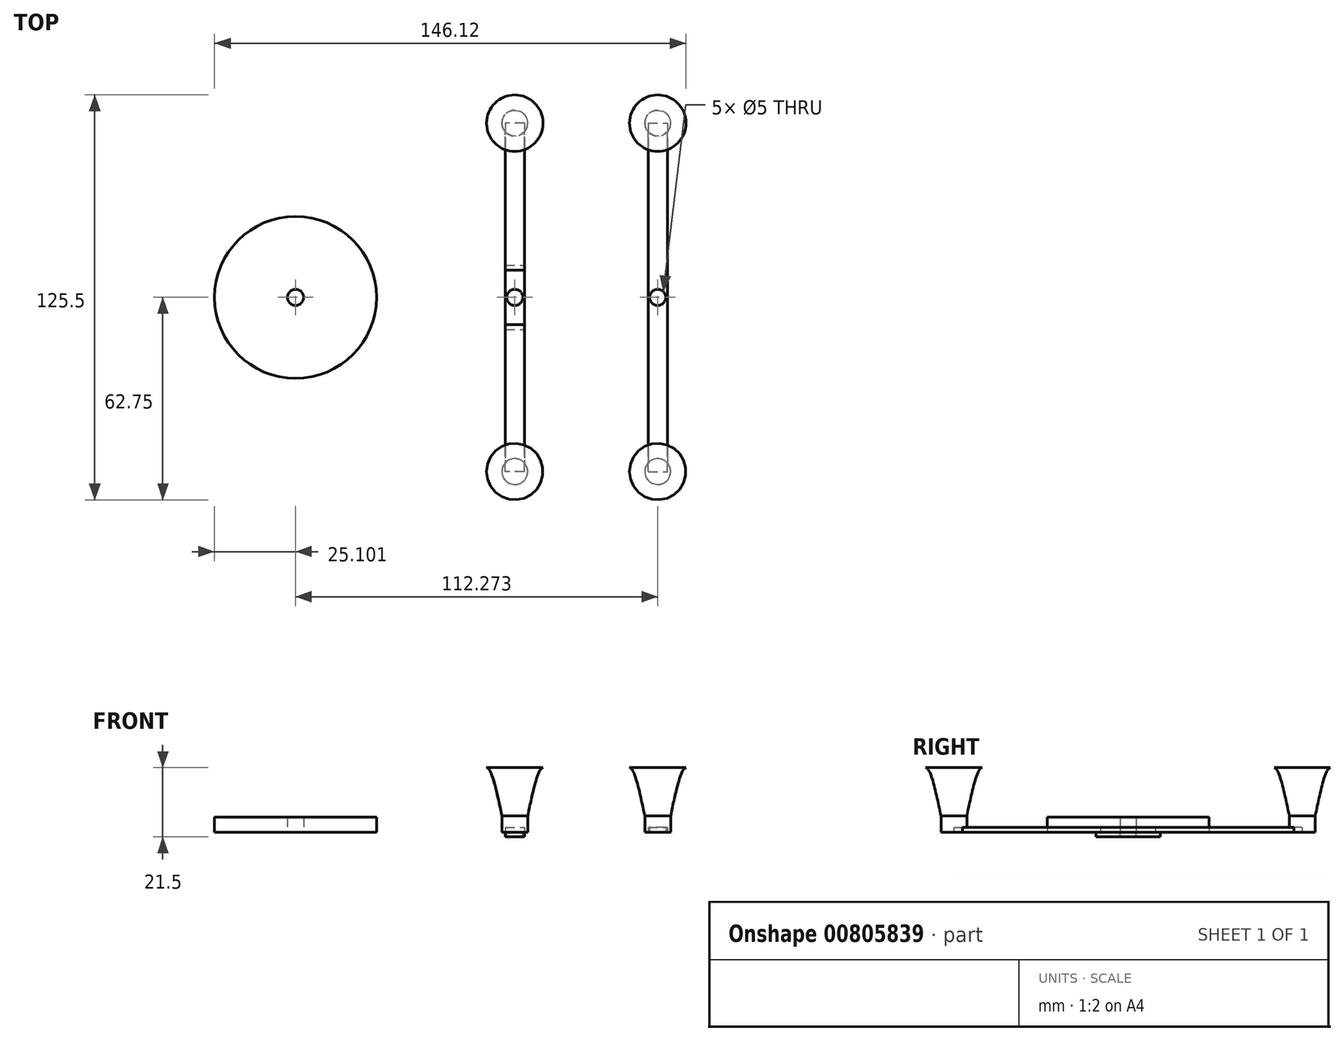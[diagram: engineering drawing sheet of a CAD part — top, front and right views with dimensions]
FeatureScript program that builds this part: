
annotation { "Feature Type Name" : "Feature", "Feature Type Description" : "" }
export const myFeature = defineFeature(function(context is Context, id is Id, definition is map)
    precondition{}
    {
        {
            var Q0;
            Q0=qCreatedBy(makeId("Top.planeOp"),FACE);
            var sketch = newSketch(context, id + "F0", { "sketchPlane" : qUnion([Q0])});
            skLineSegment(sketch, "E0.bottom", {"start": v(3, -54) * mm, "end": v(-3, -54) * mm});
            skLineSegment(sketch, "E0.top", {"start": v(3, 54) * mm, "end": v(-3, 54) * mm});
            skLineSegment(sketch, "E0.left", {"start": v(3, -54) * mm, "end": v(3, 54) * mm});
            skLineSegment(sketch, "E0.right", {"start": v(-3, -54) * mm, "end": v(-3, 54) * mm});
            skPoint(sketch, "E0.middle", {"position": v(0, 0) * mm});
            skCircle(sketch, "E1", {"center": v(0, 0) * mm, "radius": 2.5 * mm});
            skLineSegment(sketch, "E2", {"start": v(-3, 10) * mm, "end": v(3, 10) * mm});
            skLineSegment(sketch, "E3.MirrorCS", {"start": v(-3, -10) * mm, "end": v(3, -10) * mm});
            skLineSegment(sketch, "E4", {"start": v(-3, 8.5) * mm, "end": v(3, 8.5) * mm});
            skLineSegment(sketch, "E5.MirrorCS", {"start": v(-3, -8.5) * mm, "end": v(3, -8.5) * mm});
            skLineSegment(sketch, "E6.bottom", {"start": v(41.3, -54) * mm, "end": v(47.3, -54) * mm});
            skLineSegment(sketch, "E6.top", {"start": v(41.3, 54) * mm, "end": v(47.3, 54) * mm});
            skLineSegment(sketch, "E6.left", {"start": v(41.3, -54) * mm, "end": v(41.3, 54) * mm});
            skLineSegment(sketch, "E6.right", {"start": v(47.3, -54) * mm, "end": v(47.3, 54) * mm});
            skPoint(sketch, "E6.middle", {"position": v(44.3, 0) * mm});
            skCircle(sketch, "E7", {"center": v(44.3, 0) * mm, "radius": 2.5 * mm});
            skCircle(sketch, "E8", {"center": v(-67.97, 0) * mm, "radius": 25.1 * mm});
            skCircle(sketch, "E9", {"center": v(-67.97, 0) * mm, "radius": 2.5 * mm});
            skCircle(sketch, "E10", {"center": v(44.3, 54) * mm, "radius": 4 * mm});
            skCircle(sketch, "E11", {"center": v(0, 54) * mm, "radius": 4 * mm});
            skSolve(sketch);
        }
        {
            var Q0;
            {var subQ0=sQuery(id+"F0.wireOp",EDGE,"E0.top");Q0=makeQuery(id+"F0.imprint","IMPRINT",FACE,{"disambiguationData":[TD([[makeQuery(id+"F0.imprint","IMPRINT",EDGE,{"derivedFrom":subQ0}),1.0]])]});}
            var Q1;
            {var subQ0=sQuery(id+"F0.wireOp",EDGE,"E0.bottom");Q1=makeQuery(id+"F0.imprint","IMPRINT",FACE,{"disambiguationData":[TD([[makeQuery(id+"F0.imprint","IMPRINT",EDGE,{"derivedFrom":subQ0}),-1.0]])]});}
            var Q2;
            {var subQ0=sQuery(id+"F0.wireOp",EDGE,"E2");Q2=makeQuery(id+"F0.imprint","IMPRINT",FACE,{"disambiguationData":[TD([[makeQuery(id+"F0.imprint","IMPRINT",EDGE,{"derivedFrom":subQ0}),-1.0]])]});}
            var Q3;
            {var subQ0=sQuery(id+"F0.wireOp",EDGE,"E3.MirrorCS");Q3=makeQuery(id+"F0.imprint","IMPRINT",FACE,{"disambiguationData":[TD([[makeQuery(id+"F0.imprint","IMPRINT",EDGE,{"derivedFrom":subQ0}),1.0]])]});}
            var Q4;
            Q4=makeQuery(id+"F0.imprint","IMPRINT",FACE,{"disambiguationData":[TD([[makeQuery(id+"F0.imprint","IMPRINT",EDGE,{"derivedFrom":sQuery(id+"F0.wireOp",EDGE,"E6.bottom")}),1.0]])]});
            var Q5;
            {var subQ0=sQuery(id+"F0.wireOp",EDGE,"E6.top");Q5=makeQuery(id+"F0.imprint","IMPRINT",FACE,{"disambiguationData":[TD([[makeQuery(id+"F0.imprint","IMPRINT",EDGE,{"derivedFrom":subQ0}),1.0]])]});}
            var Q6;
            {var subQ0=sQuery(id+"F0.wireOp",EDGE,"E6.top");Q6=makeQuery(id+"F0.imprint","IMPRINT",FACE,{"disambiguationData":[TD([[makeQuery(id+"F0.imprint","IMPRINT",EDGE,{"derivedFrom":subQ0}),-1.0]])]});}
            var Q7;
            {var subQ0=sQuery(id+"F0.wireOp",EDGE,"E2");Q7=makeQuery(id+"F0.imprint","IMPRINT",FACE,{"disambiguationData":[TD([[makeQuery(id+"F0.imprint","IMPRINT",EDGE,{"derivedFrom":subQ0}),1.0]])]});}
            var Q8;
            {var subQ0=sQuery(id+"F0.wireOp",EDGE,"E0.top");Q8=makeQuery(id+"F0.imprint","IMPRINT",FACE,{"disambiguationData":[TD([[makeQuery(id+"F0.imprint","IMPRINT",EDGE,{"derivedFrom":subQ0}),-1.0]])]});}
            extrude(context, id + "F1", {"entities" : qUnion([Q0, Q1, Q2, Q3, Q4, Q5, Q6, Q7, Q8]), "depth" : 1.5 * mm, "offsetDistance" : 25 * mm});
        }
        {
            var Q0;
            {var subQ0=sQuery(id+"F0.wireOp",EDGE,"E2");Q0=makeQuery(id+"F0.imprint","IMPRINT",FACE,{"disambiguationData":[TD([[makeQuery(id+"F0.imprint","IMPRINT",EDGE,{"derivedFrom":subQ0}),-1.0]])]});}
            var Q1;
            Q1=makeQuery(id+"F0.imprint","IMPRINT",FACE,{"disambiguationData":[TD([[makeQuery(id+"F0.imprint","IMPRINT",EDGE,{"derivedFrom":sQuery(id+"F0.wireOp",EDGE,"E1")}),-1.0]])]});
            var Q2;
            {var subQ0=sQuery(id+"F0.wireOp",EDGE,"E3.MirrorCS");Q2=makeQuery(id+"F0.imprint","IMPRINT",FACE,{"disambiguationData":[TD([[makeQuery(id+"F0.imprint","IMPRINT",EDGE,{"derivedFrom":subQ0}),1.0]])]});}
            extrude(context, id + "F2", {"entities" : qUnion([Q0, Q1, Q2]), "operationType" : NewBodyOperationType.ADD, "oppositeDirection" : true, "depth" : 1.5 * mm, "offsetDistance" : 25 * mm});
        }
        {
            var Q0;
            Q0=makeQuery(id+"F1.opExtrude","CAP_FACE",FACE,{"disambiguationData":[OSD([sQuery(id+"F0.wireOp",EDGE,"E6.bottom"),sQuery(id+"F0.wireOp",EDGE,"E6.left"),sQuery(id+"F0.wireOp",EDGE,"E6.right"),sQuery(id+"F0.wireOp",EDGE,"E7"),sQuery(id+"F0.wireOp",EDGE,"E10")])],"isStart":true});
            cPlane(context, id + "F3", {"entities" : qUnion([Q0]), "cplaneType" : CPlaneType.OFFSET, "offset" : 20 * mm, "oppositeDirection" : true, "width" : 150 * mm, "height" : 150 * mm});
        }
        {
            var Q0;
            Q0=qCreatedBy(id+"F3.planeOp",FACE);
            var sketch = newSketch(context, id + "F4", { "sketchPlane" : qUnion([Q0])});
            skCircle(sketch, "E12", {"center": v(44.3, -54) * mm, "radius": 8.75 * mm});
            skCircle(sketch, "E13", {"center": v(0, -54) * mm, "radius": 8.75 * mm});
            skSolve(sketch);
        }
        {
            var Q0;
            {var subQ0=sQuery(id+"F0.wireOp",EDGE,"E6.top");Q0=makeQuery(id+"F0.imprint","IMPRINT",FACE,{"disambiguationData":[TD([[makeQuery(id+"F0.imprint","IMPRINT",EDGE,{"derivedFrom":subQ0}),1.0]])]});}
            var Q1;
            {var subQ0=sQuery(id+"F0.wireOp",EDGE,"E6.top");Q1=makeQuery(id+"F0.imprint","IMPRINT",FACE,{"disambiguationData":[TD([[makeQuery(id+"F0.imprint","IMPRINT",EDGE,{"derivedFrom":subQ0}),-1.0]])]});}
            var Q2;
            {var subQ0=sQuery(id+"F0.wireOp",EDGE,"E0.top");Q2=makeQuery(id+"F0.imprint","IMPRINT",FACE,{"disambiguationData":[TD([[makeQuery(id+"F0.imprint","IMPRINT",EDGE,{"derivedFrom":subQ0}),-1.0]])]});}
            var Q3;
            {var subQ0=sQuery(id+"F0.wireOp",EDGE,"E0.top");Q3=makeQuery(id+"F0.imprint","IMPRINT",FACE,{"disambiguationData":[TD([[makeQuery(id+"F0.imprint","IMPRINT",EDGE,{"derivedFrom":subQ0}),1.0]])]});}
            extrude(context, id + "F5", {"entities" : qUnion([Q0, Q1, Q2, Q3]), "operationType" : NewBodyOperationType.ADD, "depth" : 5 * mm, "offsetDistance" : 25 * mm});
        }
        {
            var Q0;
            Q0=makeQuery(id+"F4.imprint","IMPRINT",FACE,{"disambiguationData":[TD([[makeQuery(id+"F4.imprint","IMPRINT",EDGE,{"derivedFrom":sQuery(id+"F4.wireOp",EDGE,"E12")}),1.0]])]});
            var Q1;
            Q1=makeQuery(id+"F5.opExtrude","CAP_FACE",FACE,{"disambiguationData":[OSD([sQuery(id+"F0.wireOp",EDGE,"E10")])],"isStart":false});
            loft(context, id + "F6", {"operationType" : NewBodyOperationType.ADD, "startCondition" : LoftEndDerivativeType.TANGENT_TO_PROFILE, "startMagnitude" : 1, "sheetProfilesArray" : [{ "sheetProfileEntities" : qUnion([Q0]) }, { "sheetProfileEntities" : qUnion([Q1]) }]});
        }
        {
            var Q0;
            Q0=makeQuery(id+"F1.opExtrude","SWEPT_BODY",BODY,{"disambiguationData":[OSD([sQuery(id+"F0.wireOp",EDGE,"E6.bottom"),sQuery(id+"F0.wireOp",EDGE,"E6.left"),sQuery(id+"F0.wireOp",EDGE,"E6.right"),sQuery(id+"F0.wireOp",EDGE,"E7"),sQuery(id+"F0.wireOp",EDGE,"E10")])]});
            var Q1;
            Q1=qCreatedBy(makeId("Front.planeOp"),FACE);
            mirror(context, id + "F7", {"operationType" : NewBodyOperationType.ADD, "entities" : qUnion([Q0]), "mirrorPlane" : qUnion([Q1])});
        }
        {
            var Q0;
            Q0=makeQuery(id+"F4.imprint","IMPRINT",FACE,{"disambiguationData":[TD([[makeQuery(id+"F4.imprint","IMPRINT",EDGE,{"derivedFrom":sQuery(id+"F4.wireOp",EDGE,"E13")}),1.0]])]});
            var Q1;
            Q1=makeQuery(id+"F5.opExtrude","CAP_FACE",FACE,{"disambiguationData":[OSD([sQuery(id+"F0.wireOp",EDGE,"E11")])],"isStart":false});
            loft(context, id + "F8", {"operationType" : NewBodyOperationType.ADD, "startCondition" : LoftEndDerivativeType.TANGENT_TO_PROFILE, "startMagnitude" : 1, "sheetProfilesArray" : [{ "sheetProfileEntities" : qUnion([Q0]) }, { "sheetProfileEntities" : qUnion([Q1]) }]});
        }
        {
            var Q0;
            Q0=makeQuery(id+"F1.opExtrude","SWEPT_BODY",BODY,{"disambiguationData":[OSD([sQuery(id+"F0.wireOp",EDGE,"E0.bottom"),sQuery(id+"F0.wireOp",EDGE,"E0.left"),sQuery(id+"F0.wireOp",EDGE,"E0.right"),sQuery(id+"F0.wireOp",EDGE,"E5.MirrorCS")])]});
            var Q1;
            Q1=qCreatedBy(makeId("Front.planeOp"),FACE);
            mirror(context, id + "F9", {"operationType" : NewBodyOperationType.ADD, "entities" : qUnion([Q0]), "mirrorPlane" : qUnion([Q1])});
        }
        {
            var Q0;
            Q0=makeQuery(id+"F0.imprint","IMPRINT",FACE,{"disambiguationData":[TD([[makeQuery(id+"F0.imprint","IMPRINT",EDGE,{"derivedFrom":sQuery(id+"F0.wireOp",EDGE,"E8")}),1.0]])]});
            extrude(context, id + "F10", {"entities" : qUnion([Q0]), "depth" : 4.6 * mm, "offsetDistance" : 25 * mm});
        }
    });
